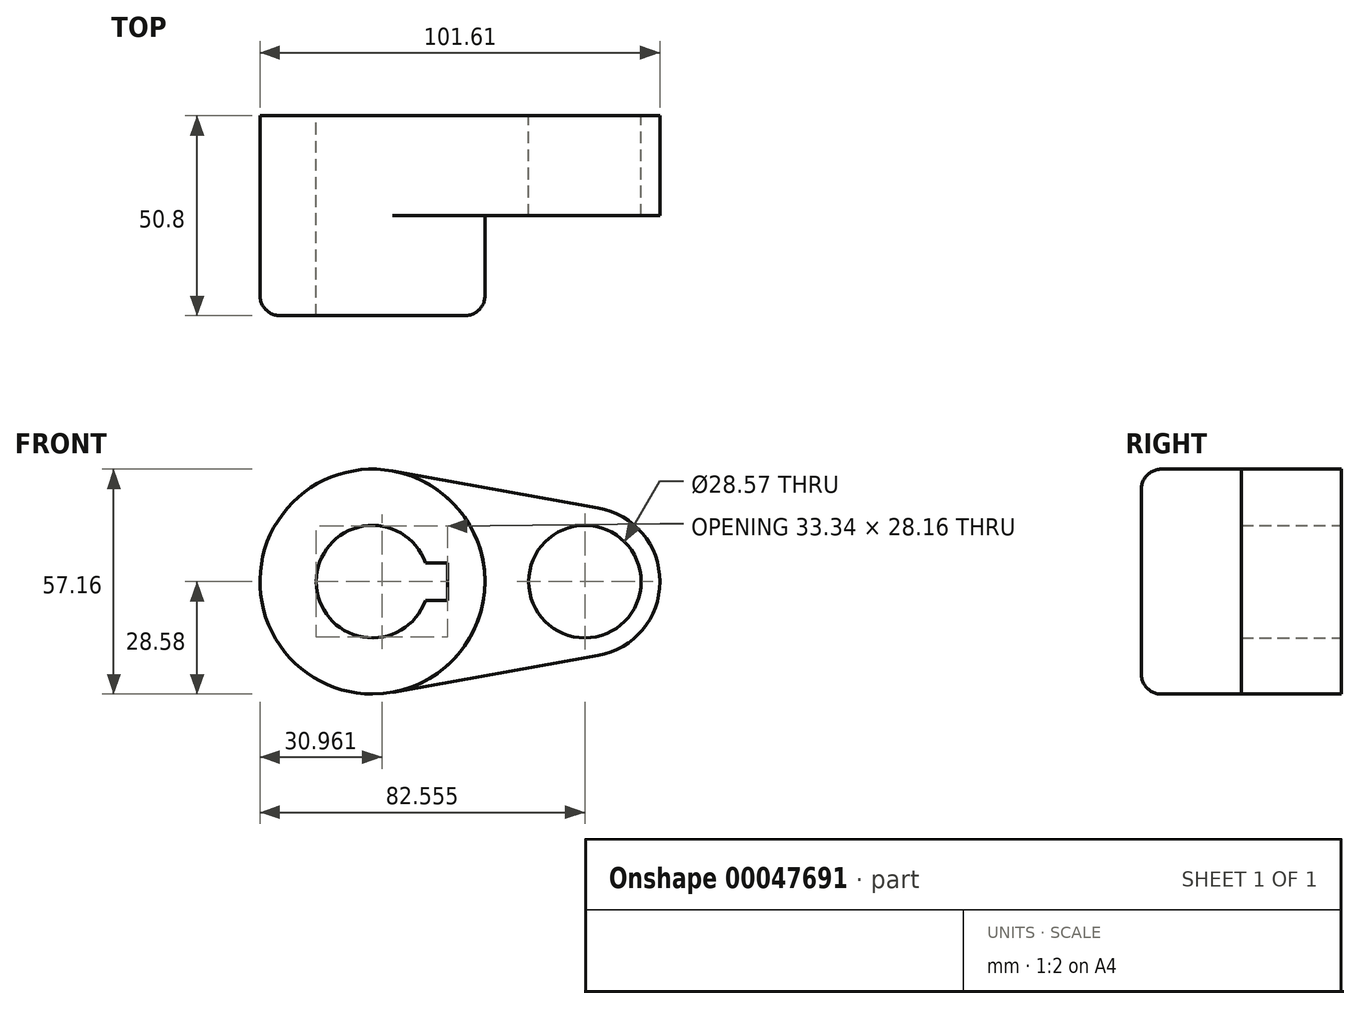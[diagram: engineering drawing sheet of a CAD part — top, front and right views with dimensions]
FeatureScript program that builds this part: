
annotation { "Feature Type Name" : "Feature", "Feature Type Description" : "" }
export const myFeature = defineFeature(function(context is Context, id is Id, definition is map)
    precondition{}
    {
        {
            var Q0;
            Q0=qCreatedBy(makeId("Front.planeOp"),FACE);
            var sketch = newSketch(context, id + "F0", { "sketchPlane" : qUnion([Q0])});
            skCircle(sketch, "E0", {"center": v(0, 0) * mm, "radius": 28.58 * mm});
            skCircle(sketch, "E1", {"center": v(53.97, 0) * mm, "radius": 19.05 * mm});
            skLineSegment(sketch, "E2", {"start": v(5.04, 28.13) * mm, "end": v(57.34, 18.75) * mm});
            skLineSegment(sketch, "E3", {"start": v(5.04, -28.13) * mm, "end": v(57.34, -18.75) * mm});
            skCircle(sketch, "E4", {"center": v(0, 0) * mm, "radius": 14.29 * mm});
            skCircle(sketch, "E5", {"center": v(53.97, 0) * mm, "radius": 14.29 * mm});
            skLineSegment(sketch, "E6.rect.bottom", {"start": v(-19.05, -4.76) * mm, "end": v(19.05, -4.76) * mm});
            skLineSegment(sketch, "E6.rect.top", {"start": v(-19.05, 4.76) * mm, "end": v(19.05, 4.76) * mm});
            skLineSegment(sketch, "E6.rect.left", {"start": v(-19.05, -4.76) * mm, "end": v(-19.05, 4.76) * mm});
            skLineSegment(sketch, "E6.rect.right", {"start": v(19.05, -4.76) * mm, "end": v(19.05, 4.76) * mm});
            skSolve(sketch);
        }
        {
            var Q0;
            {var subQ5=sQuery(id+"F0.wireOp",EDGE,"E6.rect.left");Q0=makeQuery(id+"F0.imprint","IMPRINT",FACE,{"disambiguationData":[TD([[makeQuery(id+"F0.imprint","IMPRINT",EDGE,{"derivedFrom":subQ5}),1.0]])]});}
            var Q1;
            {var subQ0=sQuery(id+"F0.wireOp",EDGE,"E6.rect.left");Q1=makeQuery(id+"F0.imprint","IMPRINT",FACE,{"disambiguationData":[TD([[makeQuery(id+"F0.imprint","IMPRINT",EDGE,{"derivedFrom":subQ0}),-1.0]])]});}
            var Q2;
            {var subQ1=sQuery(id+"F0.wireOp",EDGE,"E2");Q2=makeQuery(id+"F0.imprint","IMPRINT",FACE,{"disambiguationData":[TD([[makeQuery(id+"F0.imprint","IMPRINT",EDGE,{"derivedFrom":subQ1}),-1.0]])]});}
            var Q3;
            Q3=makeQuery(id+"F0.imprint","IMPRINT",FACE,{"disambiguationData":[TD([[makeQuery(id+"F0.imprint","IMPRINT",EDGE,{"derivedFrom":sQuery(id+"F0.wireOp",EDGE,"E5")}),-1.0]])]});
            extrude(context, id + "F1", {"entities" : qUnion([Q0, Q1, Q2, Q3]), "depth" : 25.4 * mm});
        }
        {
            var Q0;
            {var subQ5=sQuery(id+"F0.wireOp",EDGE,"E6.rect.left");Q0=makeQuery(id+"F0.imprint","IMPRINT",FACE,{"disambiguationData":[TD([[makeQuery(id+"F0.imprint","IMPRINT",EDGE,{"derivedFrom":subQ5}),1.0]])]});}
            var Q1;
            {var subQ0=sQuery(id+"F0.wireOp",EDGE,"E6.rect.left");Q1=makeQuery(id+"F0.imprint","IMPRINT",FACE,{"disambiguationData":[TD([[makeQuery(id+"F0.imprint","IMPRINT",EDGE,{"derivedFrom":subQ0}),-1.0]])]});}
            extrude(context, id + "F2", {"entities" : qUnion([Q0, Q1]), "operationType" : NewBodyOperationType.ADD, "depth" : 50.8 * mm});
        }
        {
            var Q0;
            Q0=makeQuery(id+"F2.opExtrude","CAP_EDGE",EDGE,{"disambiguationData":[OSD([sQuery(id+"F0.wireOp",EDGE,"E0")])],"isStart":false});
            fillet(context, id + "F3", {"entities" : qUnion([Q0]), "radius" : 5.08 * mm, "tangentPropagation" : true, "allowEdgeOverflow" : false});
        }
    });
